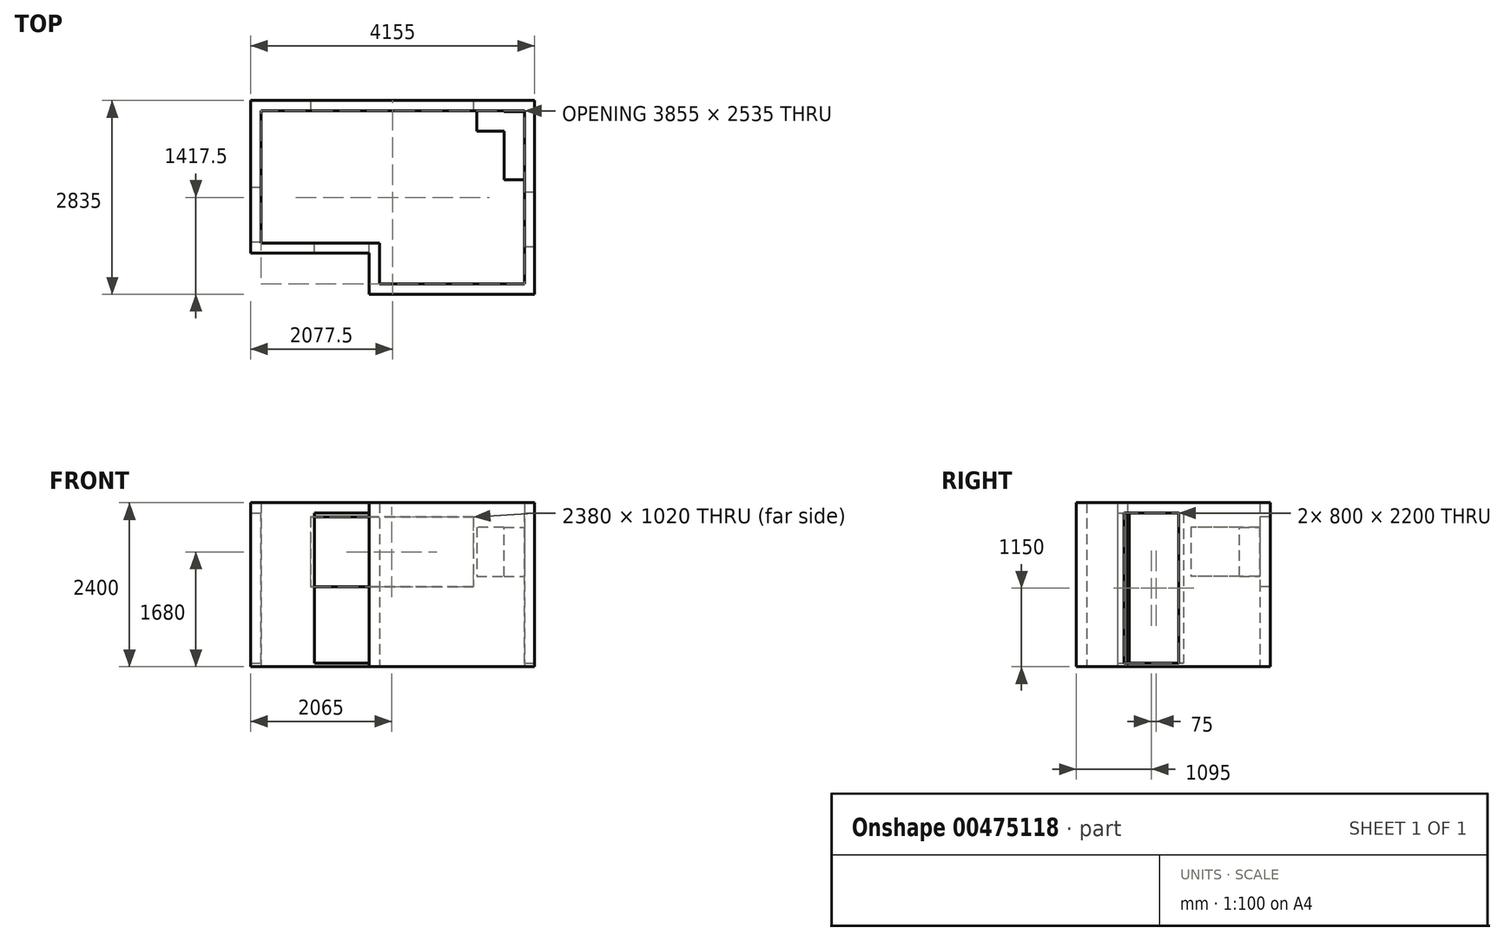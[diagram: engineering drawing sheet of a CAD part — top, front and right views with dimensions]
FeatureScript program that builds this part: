
annotation { "Feature Type Name" : "Feature", "Feature Type Description" : "" }
export const myFeature = defineFeature(function(context is Context, id is Id, definition is map)
    precondition{}
    {
        {
            var Q0;
            Q0=qCreatedBy(makeId("Top.planeOp"),FACE);
            var sketch = newSketch(context, id + "F0", { "sketchPlane" : qUnion([Q0])});
            skLineSegment(sketch, "E0", {"start": v(-147.99, -1083.6) * mm, "end": v(1972.01, -1083.6) * mm});
            skLineSegment(sketch, "E1", {"start": v(1972.01, -1083.6) * mm, "end": v(1972.01, -538.6) * mm});
            skLineSegment(sketch, "E2", {"start": v(1972.01, -538.6) * mm, "end": v(1972.01, 1451.4) * mm});
            skLineSegment(sketch, "E3", {"start": v(1972.01, 1451.4) * mm, "end": v(-1882.99, 1451.4) * mm});
            skLineSegment(sketch, "E4", {"start": v(-1882.99, 1451.4) * mm, "end": v(-1882.99, -483.6) * mm});
            skLineSegment(sketch, "E5", {"start": v(-1882.99, -483.6) * mm, "end": v(-147.99, -483.6) * mm});
            skLineSegment(sketch, "E6", {"start": v(-147.99, -483.6) * mm, "end": v(-147.99, -1083.6) * mm});
            skLineSegment(sketch, "E7.0", {"start": v(2122.01, 1601.4) * mm, "end": v(-2032.99, 1601.4) * mm});
            skLineSegment(sketch, "E7.1", {"start": v(2122.01, -278.6) * mm, "end": v(2122.01, 1601.4) * mm});
            skLineSegment(sketch, "E7.2", {"start": v(-2032.99, -633.6) * mm, "end": v(-297.99, -633.6) * mm});
            skLineSegment(sketch, "E7.3", {"start": v(-297.99, -633.6) * mm, "end": v(-297.99, -1233.6) * mm});
            skLineSegment(sketch, "E7.4", {"start": v(-297.99, -1233.6) * mm, "end": v(2122.01, -1233.6) * mm});
            skLineSegment(sketch, "E7.5", {"start": v(-2032.99, 1601.4) * mm, "end": v(-2032.99, -633.6) * mm});
            skLineSegment(sketch, "E7.6", {"start": v(2122.01, -1233.6) * mm, "end": v(2122.01, -278.6) * mm});
            skSolve(sketch);
        }
        {
            var Q0;
            Q0=makeQuery(id+"F0.imprint","IMPRINT",FACE,{"disambiguationData":[TD([[makeQuery(id+"F0.imprint","IMPRINT",EDGE,{"derivedFrom":sQuery(id+"F0.wireOp",EDGE,"E0")}),-1.0]])]});
            extrude(context, id + "F1", {"entities" : qUnion([Q0]), "depth" : 2400 * mm, "offsetDistance" : 25 * mm});
        }
        {
            var Q0;
            Q0=makeQuery(id+"F1.opExtrude","SWEPT_FACE",FACE,{"disambiguationData":[OSD([sQuery(id+"F0.wireOp",EDGE,"E7.1"),sQuery(id+"F0.wireOp",EDGE,"E7.6")])]});
            var sketch = newSketch(context, id + "F2", { "sketchPlane" : qUnion([Q0])});
            skLineSegment(sketch, "E8.bottom", {"start": v(-538.6, 50) * mm, "end": v(261.4, 50) * mm});
            skLineSegment(sketch, "E8.top", {"start": v(-538.6, 2250) * mm, "end": v(261.4, 2250) * mm});
            skLineSegment(sketch, "E8.left", {"start": v(-538.6, 50) * mm, "end": v(-538.6, 2250) * mm});
            skLineSegment(sketch, "E8.right", {"start": v(261.4, 50) * mm, "end": v(261.4, 2250) * mm});
            skSolve(sketch);
        }
        {
            var Q0;
            Q0 = qSketchRegion(id + "F2", true);
            extrude(context, id + "F3", {"entities" : qUnion([Q0]), "operationType" : NewBodyOperationType.REMOVE, "endBound" : BoundingType.UP_TO_NEXT, "oppositeDirection" : true, "depth" : 25 * mm, "offsetDistance" : 25 * mm});
        }
        {
            var Q0;
            Q0=makeQuery(id+"F1.opExtrude","SWEPT_FACE",FACE,{"disambiguationData":[OSD([sQuery(id+"F0.wireOp",EDGE,"E5")])]});
            var sketch = newSketch(context, id + "F4", { "sketchPlane" : qUnion([Q0])});
            skLineSegment(sketch, "E9.bottom", {"start": v(297.99, 50) * mm, "end": v(1097.99, 50) * mm});
            skLineSegment(sketch, "E9.top", {"start": v(297.99, 2250) * mm, "end": v(1097.99, 2250) * mm});
            skLineSegment(sketch, "E9.left", {"start": v(297.99, 50) * mm, "end": v(297.99, 2250) * mm});
            skLineSegment(sketch, "E9.right", {"start": v(1097.99, 50) * mm, "end": v(1097.99, 2250) * mm});
            skSolve(sketch);
        }
        {
            var Q0;
            Q0 = qSketchRegion(id + "F4", true);
            extrude(context, id + "F5", {"entities" : qUnion([Q0]), "operationType" : NewBodyOperationType.REMOVE, "endBound" : BoundingType.UP_TO_NEXT, "oppositeDirection" : true, "depth" : 25 * mm, "offsetDistance" : 25 * mm});
        }
        {
            var Q0;
            Q0=makeQuery(id+"F1.opExtrude","SWEPT_FACE",FACE,{"disambiguationData":[OSD([sQuery(id+"F0.wireOp",EDGE,"E4")])]});
            var sketch = newSketch(context, id + "F6", { "sketchPlane" : qUnion([Q0])});
            skLineSegment(sketch, "E10.bottom", {"start": v(-463.6, 50) * mm, "end": v(336.4, 50) * mm});
            skLineSegment(sketch, "E10.top", {"start": v(-463.6, 2250) * mm, "end": v(336.4, 2250) * mm});
            skLineSegment(sketch, "E10.left", {"start": v(-463.6, 50) * mm, "end": v(-463.6, 2250) * mm});
            skLineSegment(sketch, "E10.right", {"start": v(336.4, 50) * mm, "end": v(336.4, 2250) * mm});
            skSolve(sketch);
        }
        {
            var Q0;
            Q0 = qSketchRegion(id + "F6", true);
            extrude(context, id + "F7", {"entities" : qUnion([Q0]), "operationType" : NewBodyOperationType.REMOVE, "endBound" : BoundingType.UP_TO_NEXT, "oppositeDirection" : true, "depth" : 25 * mm, "offsetDistance" : 25 * mm});
        }
        {
            var Q0;
            Q0=makeQuery(id+"F1.opExtrude","SWEPT_FACE",FACE,{"disambiguationData":[OSD([sQuery(id+"F0.wireOp",EDGE,"E3")])]});
            var sketch = newSketch(context, id + "F8", { "sketchPlane" : qUnion([Q0])});
            skLineSegment(sketch, "E11.bottom", {"start": v(-1157.99, 2190) * mm, "end": v(1222.01, 2190) * mm});
            skLineSegment(sketch, "E11.top", {"start": v(-1157.99, 1170) * mm, "end": v(1222.01, 1170) * mm});
            skLineSegment(sketch, "E11.left", {"start": v(-1157.99, 2190) * mm, "end": v(-1157.99, 1170) * mm});
            skLineSegment(sketch, "E11.right", {"start": v(1222.01, 2190) * mm, "end": v(1222.01, 1170) * mm});
            skSolve(sketch);
        }
        {
            var Q0;
            Q0 = qSketchRegion(id + "F8", true);
            extrude(context, id + "F9", {"entities" : qUnion([Q0]), "operationType" : NewBodyOperationType.REMOVE, "endBound" : BoundingType.UP_TO_NEXT, "oppositeDirection" : true, "depth" : 25 * mm, "offsetDistance" : 25 * mm});
        }
        {
            var Q0;
            Q0=qCreatedBy(makeId("Top.planeOp"),FACE);
            var sketch = newSketch(context, id + "F10", { "sketchPlane" : qUnion([Q0])});
            skLineSegment(sketch, "E12.bottom", {"start": v(-257.99, 1441.4) * mm, "end": v(-257.99, 1441.4) * mm});
            skLineSegment(sketch, "E12.top", {"start": v(-257.99, 881.4) * mm, "end": v(-257.99, 881.4) * mm});
            skLineSegment(sketch, "E12.left", {"start": v(-257.99, 1441.4) * mm, "end": v(-257.99, 881.4) * mm});
            skLineSegment(sketch, "E12.right", {"start": v(-257.99, 1441.4) * mm, "end": v(-257.99, 881.4) * mm});
            skLineSegment(sketch, "E13.bottom", {"start": v(-257.99, 1441.4) * mm, "end": v(342.01, 1441.4) * mm});
            skLineSegment(sketch, "E13.top", {"start": v(-257.99, 881.4) * mm, "end": v(342.01, 881.4) * mm});
            skLineSegment(sketch, "E13.right", {"start": v(342.01, 1441.4) * mm, "end": v(342.01, 881.4) * mm});
            skLineSegment(sketch, "E14.bottom", {"start": v(342.01, 1441.4) * mm, "end": v(942.01, 1441.4) * mm});
            skLineSegment(sketch, "E14.top", {"start": v(342.01, 881.4) * mm, "end": v(942.01, 881.4) * mm});
            skLineSegment(sketch, "E14.right", {"start": v(942.01, 1441.4) * mm, "end": v(942.01, 881.4) * mm});
            skLineSegment(sketch, "E15.bottom", {"start": v(-125.99, -496.9) * mm, "end": v(274.01, -496.9) * mm});
            skLineSegment(sketch, "E15.top", {"start": v(-125.99, -1056.9) * mm, "end": v(274.01, -1056.9) * mm});
            skLineSegment(sketch, "E15.left", {"start": v(-125.99, -496.9) * mm, "end": v(-125.99, -1056.9) * mm});
            skLineSegment(sketch, "E15.right", {"start": v(274.01, -496.9) * mm, "end": v(274.01, -1056.9) * mm});
            skLineSegment(sketch, "E16.bottom", {"start": v(274.01, -496.9) * mm, "end": v(574.01, -496.9) * mm});
            skLineSegment(sketch, "E16.top", {"start": v(274.01, -1056.9) * mm, "end": v(574.01, -1056.9) * mm});
            skLineSegment(sketch, "E16.right", {"start": v(574.01, -496.9) * mm, "end": v(574.01, -1056.9) * mm});
            skLineSegment(sketch, "E17.bottom", {"start": v(574.01, -496.9) * mm, "end": v(1174.01, -496.9) * mm});
            skLineSegment(sketch, "E17.top", {"start": v(574.01, -1056.9) * mm, "end": v(1174.01, -1056.9) * mm});
            skLineSegment(sketch, "E17.right", {"start": v(1174.01, -496.9) * mm, "end": v(1174.01, -1056.9) * mm});
            skLineSegment(sketch, "E18.bottom", {"start": v(1174.01, -496.9) * mm, "end": v(1474.01, -496.9) * mm});
            skLineSegment(sketch, "E18.top", {"start": v(1174.01, -1056.9) * mm, "end": v(1474.01, -1056.9) * mm});
            skLineSegment(sketch, "E18.right", {"start": v(1474.01, -496.9) * mm, "end": v(1474.01, -1056.9) * mm});
            skLineSegment(sketch, "E19.bottom", {"start": v(1474.01, -496.9) * mm, "end": v(1874.01, -496.9) * mm});
            skLineSegment(sketch, "E19.top", {"start": v(1474.01, -1056.9) * mm, "end": v(1874.01, -1056.9) * mm});
            skLineSegment(sketch, "E19.right", {"start": v(1874.01, -496.9) * mm, "end": v(1874.01, -1056.9) * mm});
            skLineSegment(sketch, "E20.bottom", {"start": v(-1799.99, 1441.4) * mm, "end": v(-1179.99, 1441.4) * mm});
            skLineSegment(sketch, "E20.top", {"start": v(-1799.99, 706.4) * mm, "end": v(-1179.99, 706.4) * mm});
            skLineSegment(sketch, "E20.left", {"start": v(-1799.99, 1441.4) * mm, "end": v(-1799.99, 706.4) * mm});
            skLineSegment(sketch, "E20.right", {"start": v(-1179.99, 1441.4) * mm, "end": v(-1179.99, 706.4) * mm});
            skLineSegment(sketch, "E21.bottom", {"start": v(942.01, 1441.4) * mm, "end": v(1842.01, 1441.4) * mm});
            skLineSegment(sketch, "E21.top", {"start": v(942.01, 881.4) * mm, "end": v(1842.01, 881.4) * mm});
            skLineSegment(sketch, "E21.right", {"start": v(1842.01, 1441.4) * mm, "end": v(1842.01, 881.4) * mm});
            skLineSegment(sketch, "E22.top", {"start": v(1402.01, 463.4) * mm, "end": v(1962.01, 463.4) * mm});
            skLineSegment(sketch, "E22.right", {"start": v(1962.01, 863.4) * mm, "end": v(1962.01, 463.4) * mm});
            skLineSegment(sketch, "E23", {"start": v(1402.01, 463.4) * mm, "end": v(1402.01, 863.4) * mm});
            skLineSegment(sketch, "E24", {"start": v(1402.01, 863.4) * mm, "end": v(1962.01, 863.4) * mm});
            skLineSegment(sketch, "E25.bottom", {"start": v(-257.99, 1441.4) * mm, "end": v(-1157.99, 1441.4) * mm});
            skLineSegment(sketch, "E25.top", {"start": v(-257.99, 881.4) * mm, "end": v(-1157.99, 881.4) * mm});
            skLineSegment(sketch, "E25.right", {"start": v(-1157.99, 1441.4) * mm, "end": v(-1157.99, 881.4) * mm});
            skSolve(sketch);
        }
        {
            var Q0;
            Q0=makeQuery(id+"F1.opExtrude","SWEPT_FACE",FACE,{"disambiguationData":[OSD([sQuery(id+"F0.wireOp",EDGE,"E1"),sQuery(id+"F0.wireOp",EDGE,"E2")])]});
            var sketch = newSketch(context, id + "F11", { "sketchPlane" : qUnion([Q0])});
            skLineSegment(sketch, "E26.bottom", {"start": v(-1441.4, 2040.34) * mm, "end": v(-841.4, 2040.34) * mm});
            skLineSegment(sketch, "E26.top", {"start": v(-1441.4, 1320.34) * mm, "end": v(-841.4, 1320.34) * mm});
            skLineSegment(sketch, "E26.left", {"start": v(-1441.4, 2040.34) * mm, "end": v(-1441.4, 1320.34) * mm});
            skLineSegment(sketch, "E26.right", {"start": v(-841.4, 2040.34) * mm, "end": v(-841.4, 1320.34) * mm});
            skLineSegment(sketch, "E27.bottom", {"start": v(-841.4, 2040.34) * mm, "end": v(-441.4, 2040.34) * mm});
            skLineSegment(sketch, "E27.top", {"start": v(-841.4, 1320.34) * mm, "end": v(-441.4, 1320.34) * mm});
            skLineSegment(sketch, "E27.right", {"start": v(-441.4, 2040.34) * mm, "end": v(-441.4, 1320.34) * mm});
            skSolve(sketch);
        }
        {
            var Q0;
            Q0 = qSketchRegion(id + "F11", true);
            extrude(context, id + "F12", {"entities" : qUnion([Q0]), "operationType" : NewBodyOperationType.ADD, "depth" : 300 * mm, "offsetDistance" : 25 * mm});
        }
        {
            var Q0;
            Q0=makeQuery(id+"F1.opExtrude","SWEPT_FACE",FACE,{"disambiguationData":[OSD([sQuery(id+"F0.wireOp",EDGE,"E3")])]});
            var sketch = newSketch(context, id + "F13", { "sketchPlane" : qUnion([Q0])});
            skLineSegment(sketch, "E28.top", {"start": v(1272.01, 1320.34) * mm, "end": v(1672.01, 1320.34) * mm});
            skLineSegment(sketch, "E28.left", {"start": v(1272.01, 2040.34) * mm, "end": v(1272.01, 1320.34) * mm});
            skLineSegment(sketch, "E29", {"start": v(1672.01, 1320.34) * mm, "end": v(1672.01, 2040.34) * mm});
            skLineSegment(sketch, "E30", {"start": v(1672.01, 2040.34) * mm, "end": v(1272.01, 2040.34) * mm});
            skSolve(sketch);
        }
        {
            var Q0;
            Q0 = qSketchRegion(id + "F13", true);
            extrude(context, id + "F14", {"entities" : qUnion([Q0]), "operationType" : NewBodyOperationType.ADD, "depth" : 300 * mm, "offsetDistance" : 25 * mm});
        }
    });
